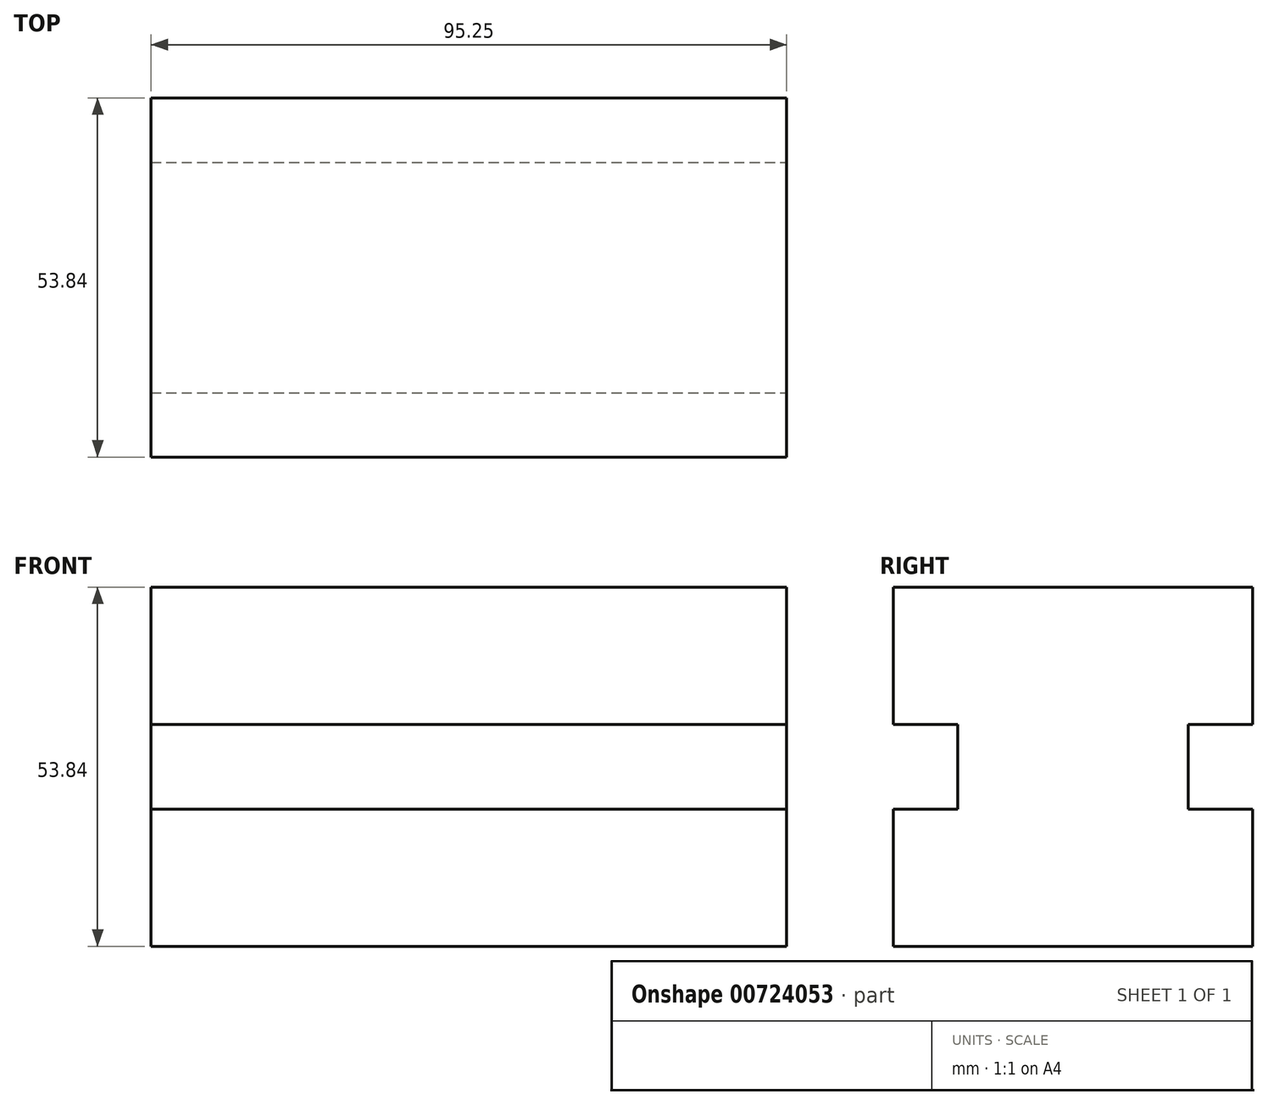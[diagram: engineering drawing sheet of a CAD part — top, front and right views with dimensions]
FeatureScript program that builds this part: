
annotation { "Feature Type Name" : "Feature", "Feature Type Description" : "" }
export const myFeature = defineFeature(function(context is Context, id is Id, definition is map)
    precondition{}
    {
        {
            var Q0;
            Q0=qCreatedBy(makeId("Right.planeOp"),FACE);
            var sketch = newSketch(context, id + "F0", { "sketchPlane" : qUnion([Q0])});
            skLineSegment(sketch, "E0.bottom", {"start": v(26.92, -26.92) * mm, "end": v(-26.92, -26.92) * mm});
            skLineSegment(sketch, "E0.top", {"start": v(26.92, 26.92) * mm, "end": v(-26.92, 26.92) * mm});
            skLineSegment(sketch, "E0.left", {"start": v(26.92, -26.92) * mm, "end": v(26.92, -6.35) * mm});
            skLineSegment(sketch, "E0.right", {"start": v(-26.92, -26.92) * mm, "end": v(-26.92, -6.35) * mm});
            skPoint(sketch, "E0.middle", {"position": v(0, 0) * mm});
            skLineSegment(sketch, "E1.bottom", {"start": v(-26.92, 6.35) * mm, "end": v(-17.27, 6.35) * mm});
            skLineSegment(sketch, "E1.top", {"start": v(-26.92, -6.35) * mm, "end": v(-17.27, -6.35) * mm});
            skLineSegment(sketch, "E1.right", {"start": v(-17.27, 6.35) * mm, "end": v(-17.27, -6.35) * mm});
            skLineSegment(sketch, "E2.trimOffspring", {"start": v(-26.92, 6.35) * mm, "end": v(-26.92, 26.92) * mm});
            skLineSegment(sketch, "E3", {"start": v(0, 33.25) * mm, "end": v(0, -38.67) * mm, "construction": true});
            skLineSegment(sketch, "E4.MirrorCS", {"start": v(26.92, 6.35) * mm, "end": v(17.27, 6.35) * mm});
            skLineSegment(sketch, "E5.MirrorCS", {"start": v(17.27, 6.35) * mm, "end": v(17.27, -6.35) * mm});
            skLineSegment(sketch, "E6.MirrorCS", {"start": v(26.92, -6.35) * mm, "end": v(17.27, -6.35) * mm});
            skLineSegment(sketch, "E7.trimOffspring", {"start": v(26.92, 6.35) * mm, "end": v(26.92, 26.92) * mm});
            skSolve(sketch);
        }
        {
            var Q0;
            Q0=makeQuery(id+"F0.imprint","IMPRINT",FACE,{"disambiguationData":[TD([[makeQuery(id+"F0.imprint","IMPRINT",EDGE,{"derivedFrom":sQuery(id+"F0.wireOp",EDGE,"E0.bottom")}),-1.0]])]});
            extrude(context, id + "F1", {"entities" : qUnion([Q0]), "oppositeDirection" : true, "depth" : 95.25 * mm, "offsetDistance" : 25.4 * mm});
        }
    });
